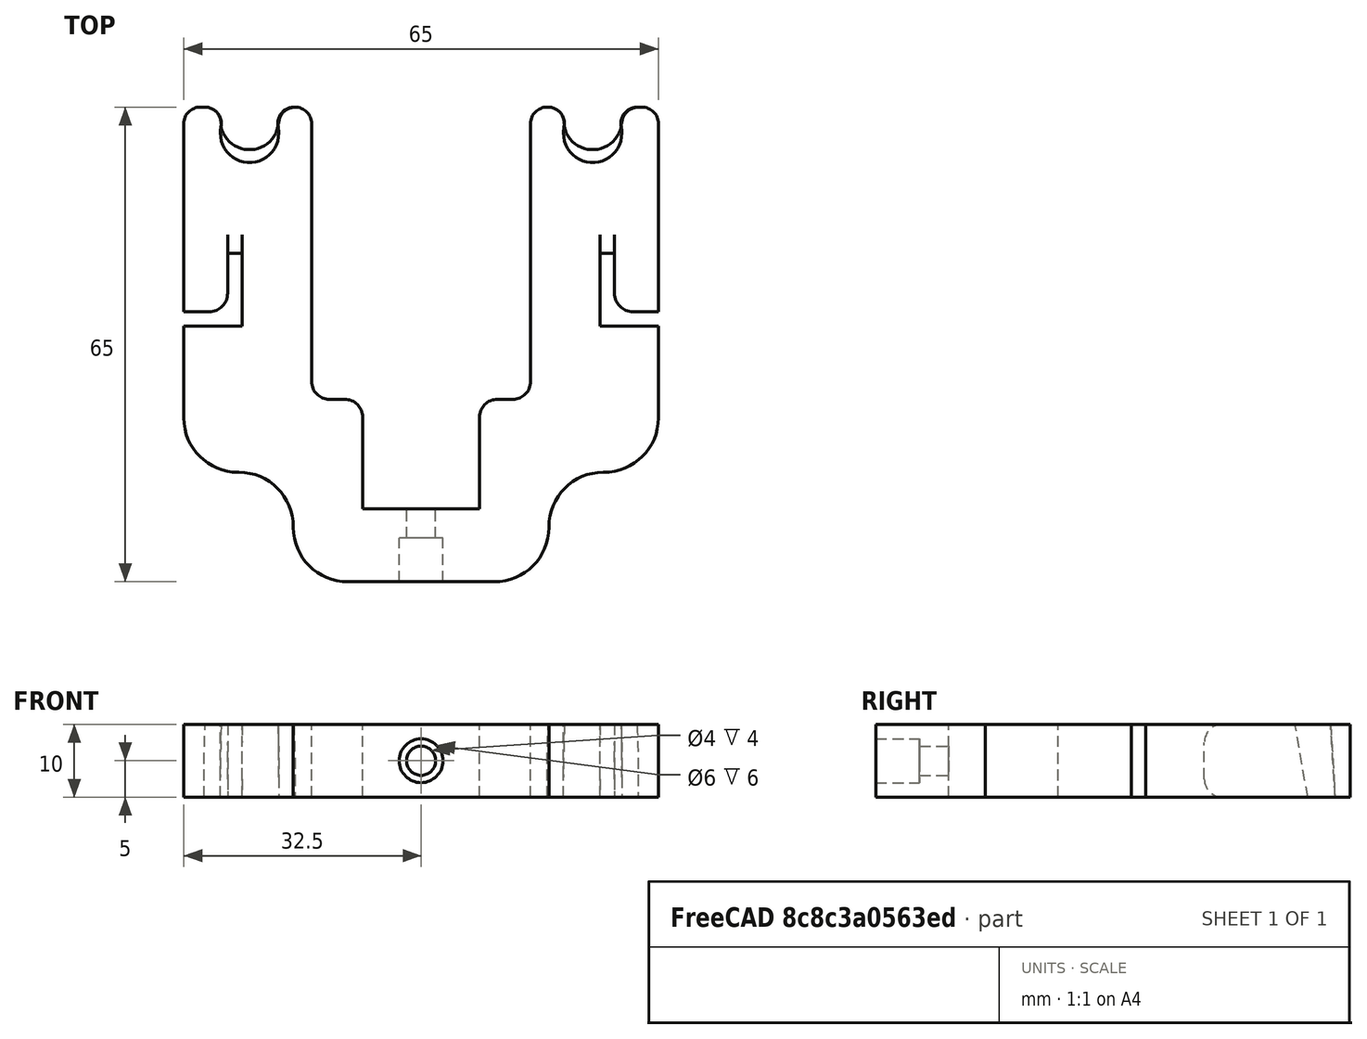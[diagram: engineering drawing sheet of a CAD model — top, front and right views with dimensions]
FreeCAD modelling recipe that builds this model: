
FCSTD DOCUMENT  (FreeCAD 0.14R3703 (Git))
Label: transport-lock
License: CC-BY 3.0
LicenseURL: http://creativecommons.org/licenses/by/3.0/
objects: Part::Cut×11, Part::Box×9, Part::Cylinder×4, Part::Fillet×4, Part::MultiFuse×1
note: 29 computed .brp shape members not serialized (recipe doc carries the construction recipe); baked Part::Feature solids carry a one-line shape summary decoded from their .brp

FEATURE [Part::Box] Box  label="Base-uncut"
  Height = 10
  Length = 65
  Width = 65
FEATURE [Part::Box] Box001  label="Z-Extrusion"
  Height = 80
  Length = 16
  Placement = pos=(24.5,10,-10) rot=(0,0,1;0rad)
  Width = 15
FEATURE [Part::Cylinder] Cylinder  label="Carbon1"
  Angle = 360
  Height = 80
  Placement = pos=(9,65,-10) rot=(1,0,0;0.174533rad)
  Radius = 4
FEATURE [Part::Cylinder] Cylinder001  label="Carbon2"
  Angle = 360
  Height = 80
  Placement = pos=(56,65,-10) rot=(1,0,0;0.174533rad)
  Radius = 4
FEATURE [Part::Box] Box002  label="Belt-Space"
  Height = 10
  Length = 30
  Placement = pos=(17.5,25,0) rot=(0,0,1;0rad)
  Width = 40
FEATURE [Part::Box] Box003  label="Cut-Off1"
  Height = 10
  Length = 15
  Width = 15
FEATURE [Part::Box] Box004  label="Cut-Off2"
  Height = 10
  Length = 15
  Placement = pos=(50,0,0) rot=(0,0,1;0rad)
  Width = 15
FEATURE [Part::Cylinder] Cylinder002  label="M3-hole"
  Angle = 360
  Height = 10
  Radius = 2
FEATURE [Part::Cylinder] Cylinder003  label="M5.5-hole"
  Angle = 360
  Height = 6
  Radius = 3
FEATURE [Part::MultiFuse] Fusion  label="Bolt-hole"
  Placement = pos=(32.5,0,5) rot=(-1,0,0;1.5708rad)
  Shapes = -> [Cylinder002,Cylinder003]
FEATURE [Part::Box] Box005  label="Rubber-band1"
  Height = 10
  Length = 2
  Placement = pos=(6,35,0) rot=(0,0,1;0rad)
  Width = 10
FEATURE [Part::Box] Box006  label="Rubber-band2"
  Height = 10
  Length = 2
  Placement = pos=(57,35,0) rot=(0,0,1;0rad)
  Width = 10
FEATURE [Part::Box] Box007  label="Rubber-band3"
  Height = 10
  Length = 8
  Placement = pos=(0,35,0) rot=(0,0,1;0rad)
  Width = 2
FEATURE [Part::Box] Box008  label="Rubber-band4"
  Height = 10
  Length = 8
  Placement = pos=(57,35,0) rot=(0,0,1;0rad)
  Width = 2
FEATURE [Part::Cut] Cut
  Base = -> Box
  Tool = -> Fusion
FEATURE [Part::Cut] Cut001
  Base = -> Cut
  Tool = -> Box008
FEATURE [Part::Cut] Cut002
  Base = -> Cut001
  Tool = -> Box007
FEATURE [Part::Cut] Cut003
  Base = -> Cut002
  Tool = -> Box006
FEATURE [Part::Cut] Cut004
  Base = -> Cut003
  Tool = -> Box005
FEATURE [Part::Cut] Cut005
  Base = -> Cut004
  Tool = -> Box001
FEATURE [Part::Cut] Cut006
  Base = -> Cut005
  Tool = -> Cylinder
FEATURE [Part::Cut] Cut007
  Base = -> Cut006
  Tool = -> Cylinder001
FEATURE [Part::Cut] Cut008
  Base = -> Cut007
  Tool = -> Box002
FEATURE [Part::Cut] Cut009
  Base = -> Cut008
  Tool = -> Box003
FEATURE [Part::Cut] Cut010  label="Base-cut"
  Base = -> Cut009
  Tool = -> Box004
FEATURE [Part::Fillet] Fillet  label="Fillet-7.45"
  Base = -> Cut010
  Edges = 6 edges r=7.45: [Edge4,Edge80,Edge88,Edge89,Edge90,Edge91]
FEATURE [Part::Fillet] Fillet001  label="Fillet-2.45"
  Base = -> Fillet
  Edges = 4 edges r=2.45: [Edge117,Edge119,Edge126,Edge128]
FEATURE [Part::Fillet] Fillet002  label="Fillet-Rubber-Band"
  Base = -> Fillet001
  Edges = 6 edges r=2.5: [Edge17,Edge36,Edge76,Edge83,Edge114,Edge121]
FEATURE [Part::Fillet] Fillet003  label="Transport-lock"
  Base = -> Fillet002
  Edges = 8 edges r=2.25: [Edge60,Edge68,Edge74,Edge81,Edge124,Edge129,Edge137,Edge141]
